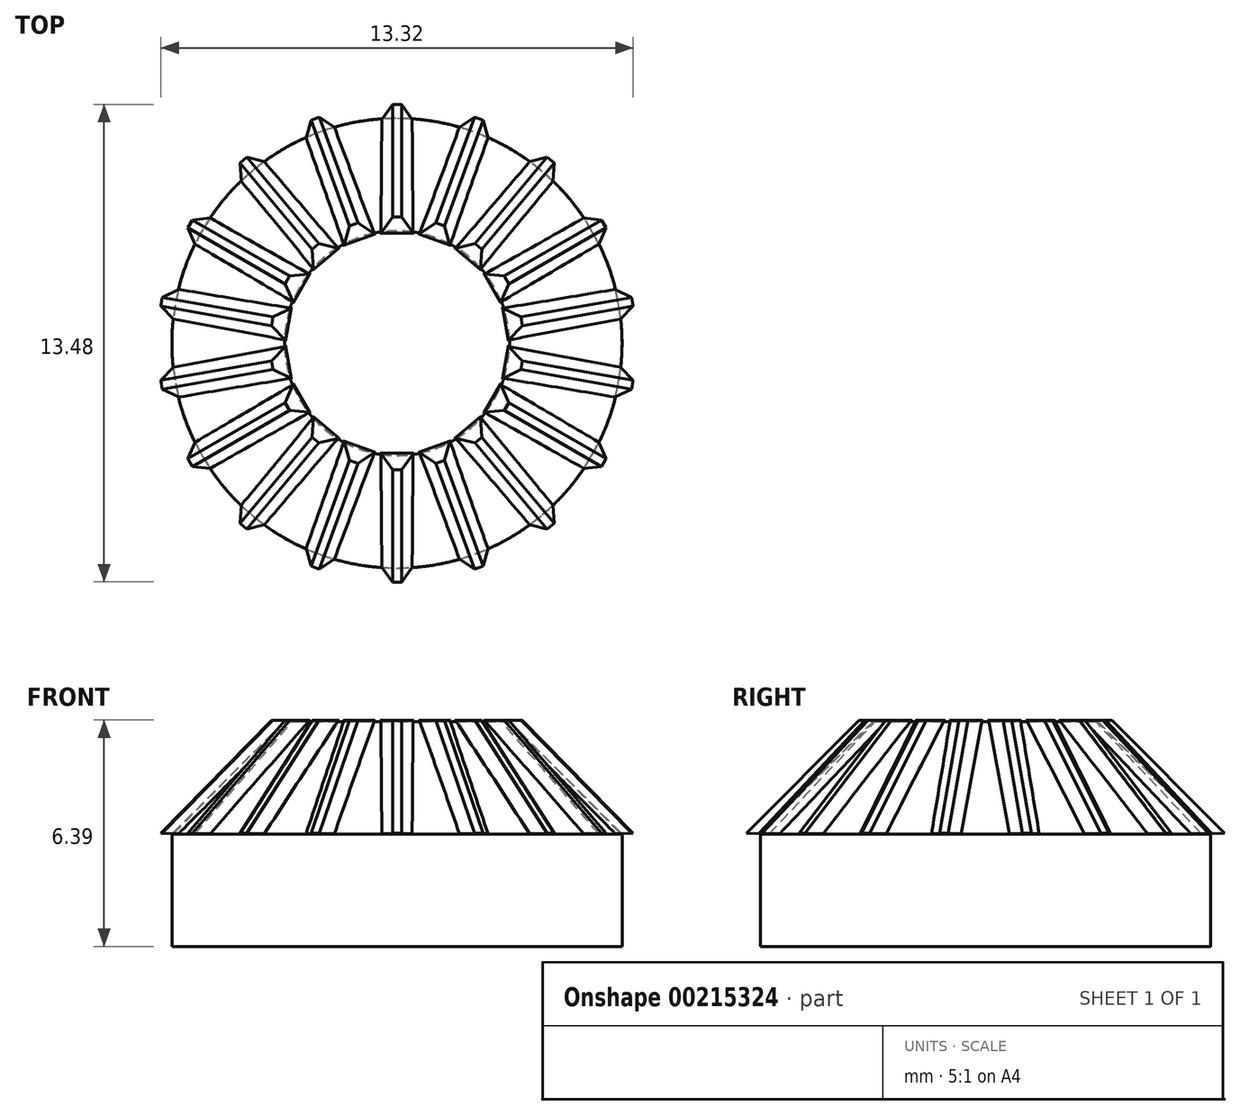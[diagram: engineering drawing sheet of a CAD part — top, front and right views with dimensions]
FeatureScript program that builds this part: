
annotation { "Feature Type Name" : "Feature", "Feature Type Description" : "" }
export const myFeature = defineFeature(function(context is Context, id is Id, definition is map)
    precondition{}
    {
        {
            var Q0;
            Q0=qCreatedBy(makeId("Top.planeOp"),FACE);
            var sketch = newSketch(context, id + "F0", { "sketchPlane" : qUnion([Q0])});
            skCircle(sketch, "E0", {"center": v(0, 0) * mm, "radius": 6.35 * mm});
            skSolve(sketch);
        }
        {
            var Q0;
            Q0=makeQuery(id+"F0.imprint","IMPRINT",FACE,{"disambiguationData":[TD([[makeQuery(id+"F0.imprint","IMPRINT",EDGE,{"derivedFrom":sQuery(id+"F0.wireOp",EDGE,"E0")}),1.0]])]});
            extrude(context, id + "F1", {"entities" : qUnion([Q0]), "depth" : 6.35 * mm});
        }
        {
            var Q0;
            Q0=makeQuery(id+"F1.opExtrude","CAP_EDGE",EDGE,{"disambiguationData":[OSD([sQuery(id+"F0.wireOp",EDGE,"E0")])],"isStart":false});
            chamfer(context, id + "F2", {"entities" : qUnion([Q0]), "width" : 3.17 * mm, "tangentPropagation" : true});
        }
        {
            var Q0;
            Q0=qCreatedBy(makeId("Right.planeOp"),FACE);
            var sketch = newSketch(context, id + "F3", { "sketchPlane" : qUnion([Q0])});
            skLineSegment(sketch, "E1", {"start": v(-6.74, 3.2) * mm, "end": v(-3.57, 6.39) * mm});
            skLineSegment(sketch, "E2", {"start": v(-6.28, 3.18) * mm, "end": v(-3.1, 6.38) * mm});
            skLineSegment(sketch, "E3", {"start": v(-3.57, 6.39) * mm, "end": v(-3.1, 6.38) * mm});
            skLineSegment(sketch, "E4", {"start": v(-6.74, 3.2) * mm, "end": v(-6.28, 3.18) * mm});
            skSolve(sketch);
        }
        {
            var Q0;
            Q0=makeQuery(id+"F3.imprint","IMPRINT",FACE,{"disambiguationData":[TD([[makeQuery(id+"F3.imprint","IMPRINT",EDGE,{"derivedFrom":sQuery(id+"F3.wireOp",EDGE,"E1")}),-1.0]])]});
            extrude(context, id + "F4", {"entities" : qUnion([Q0]), "operationType" : NewBodyOperationType.ADD, "endBound" : BoundingType.SYMMETRIC, "depth" : 1.02 * mm});
        }
        {
            var Q0;
            Q0=makeQuery(id+"F4.opExtrude","CAP_EDGE",EDGE,{"disambiguationData":[OSD([sQuery(id+"F3.wireOp",EDGE,"E1")])],"isStart":true});
            var Q1;
            Q1=makeQuery(id+"F4.opExtrude","CAP_EDGE",EDGE,{"disambiguationData":[OSD([sQuery(id+"F3.wireOp",EDGE,"E1")])],"isStart":false});
            chamfer(context, id + "F5", {"entities" : qUnion([Q0, Q1]), "width" : 0.38 * mm, "tangentPropagation" : true});
        }
        {
            var Q0;
            Q0=makeQuery(id+"F1.opExtrude","SWEPT_BODY",BODY,{"disambiguationData":[OSD([sQuery(id+"F0.wireOp",EDGE,"E0")])]});
            var Q1;
            Q1=makeQuery(id+"F2.opChamfer","BLEND_FACE",FACE,{"disambiguationData":[OSD([sQuery(id+"F0.wireOp",EDGE,"E0")])]});
            circularPattern(context, id + "F6", {"entities" : qUnion([Q0]), "axis" : qUnion([Q1]), "angle" : 360 * degree, "instanceCount" : 18, "equalSpace" : true});
        }
    });
